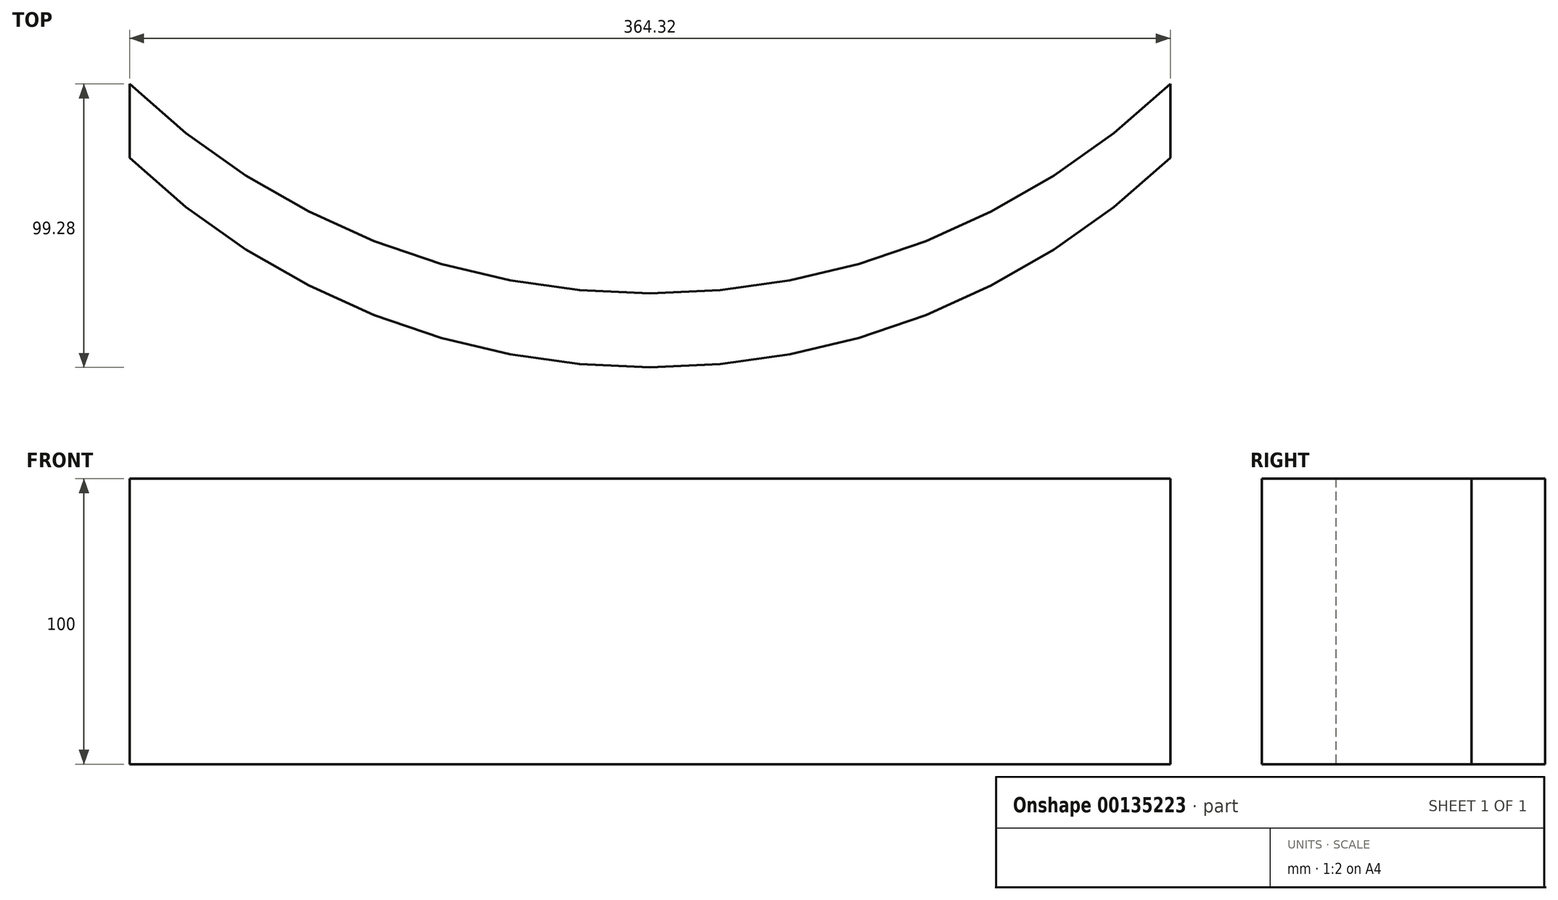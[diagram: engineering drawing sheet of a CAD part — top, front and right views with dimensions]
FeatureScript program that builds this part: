
annotation { "Feature Type Name" : "Feature", "Feature Type Description" : "" }
export const myFeature = defineFeature(function(context is Context, id is Id, definition is map)
    precondition{}
    {
        {
            var Q0;
            Q0=qCreatedBy(makeId("Top.planeOp"),FACE);
            var sketch = newSketch(context, id + "F0", { "sketchPlane" : qUnion([Q0])});
            skArc(sketch, "E0", {"start": v(-182.16, -189.43) * mm, "mid": v(0, -262.8) * mm, "end": v(182.16, -189.43) * mm});
            skLineSegment(sketch, "E1", {"start": v(-182.16, -189.43) * mm, "end": v(182.16, -189.43) * mm, "construction": true});
            skSolve(sketch);
        }
        {
            var Q0;
            Q0=qSketchRegion(id+"F0",true);
            var Q1;
            Q1=sQuery(id+"F0.wireOp",EDGE,"E0");
            extrude(context, id + "F1", {"entities" : qUnion([Q0]), "bodyType" : ToolBodyType.SURFACE, "surfaceEntities" : qUnion([Q1]), "oppositeDirection" : true, "depth" : 100 * mm});
        }
        {
            var Q0;
            Q0=makeQuery(id+"F1.opExtrude","SWEPT_BODY",BODY,{"disambiguationData":[OSD([sQuery(id+"F0.wireOp",EDGE,"E0")])]});
            transform(context, id + "F2", {"entities" : qUnion([Q0]), "transformType" : TransformType.TRANSLATION_3D, "dx" : 0 * mm, "dy" : -25.9 * mm, "dz" : 0 * mm, "makeCopy" : true});
        }
        {
            var Q0;
            Q0=makeQuery(id+"F1.opExtrude","SWEPT_FACE",FACE,{"disambiguationData":[OSD([sQuery(id+"F0.wireOp",EDGE,"E0")])]});
            var Q1;
            Q1=makeQuery(id+"F2.opPattern","COPY",FACE,{"derivedFrom":makeQuery(id+"F1.opExtrude","SWEPT_FACE",FACE,{"disambiguationData":[OSD([sQuery(id+"F0.wireOp",EDGE,"E0")])]}),"instanceName":"1"});
            loft(context, id + "F3", {"sheetProfilesArray" : [{ "sheetProfileEntities" : qUnion([Q0]) }, { "sheetProfileEntities" : qUnion([Q1]) }]});
        }
    });
